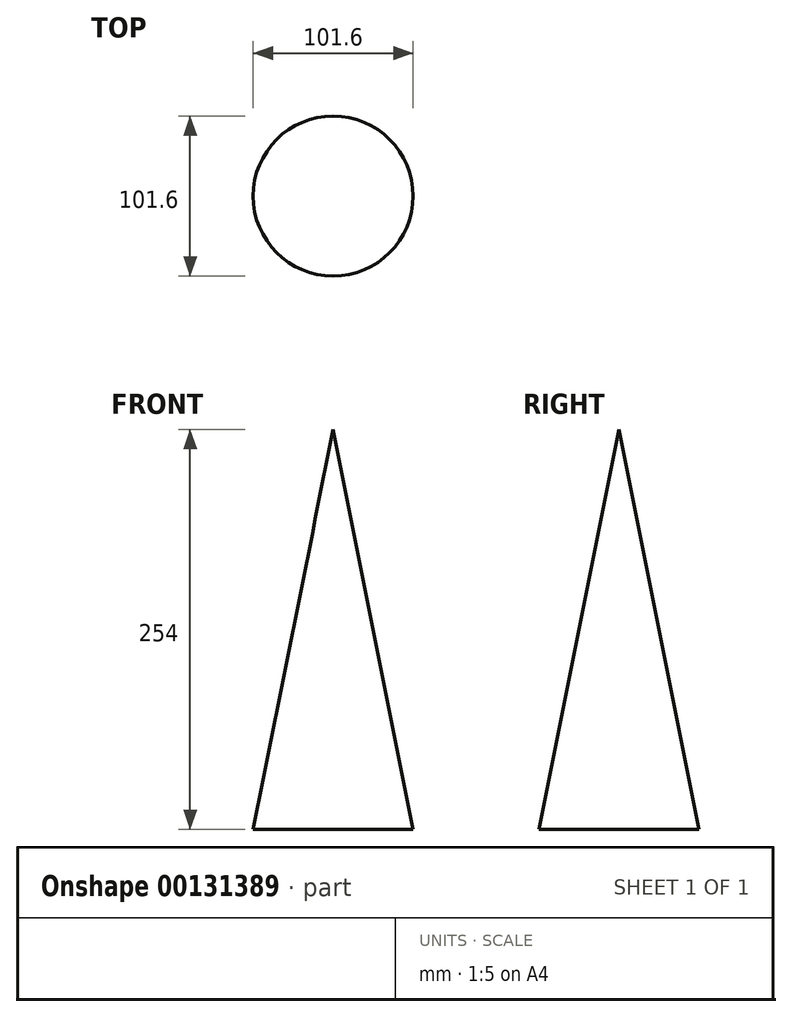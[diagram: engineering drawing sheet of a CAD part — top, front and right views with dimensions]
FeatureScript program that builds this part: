
annotation { "Feature Type Name" : "Feature", "Feature Type Description" : "" }
export const myFeature = defineFeature(function(context is Context, id is Id, definition is map)
    precondition{}
    {
        {
            var Q0;
            Q0=qCreatedBy(makeId("Front.planeOp"),FACE);
            var sketch = newSketch(context, id + "F0", { "sketchPlane" : qUnion([Q0])});
            skLineSegment(sketch, "E0", {"start": v(0, 132.51) * mm, "end": v(0, -121.49) * mm});
            skLineSegment(sketch, "E1", {"start": v(0, -121.49) * mm, "end": v(-50.8, -121.49) * mm});
            skLineSegment(sketch, "E2", {"start": v(0, 132.51) * mm, "end": v(-50.8, -121.49) * mm});
            skSolve(sketch);
        }
        {
            var Q0;
            Q0=makeQuery(id+"F0.imprint","IMPRINT",FACE,{"disambiguationData":[TD([[makeQuery(id+"F0.imprint","IMPRINT",EDGE,{"derivedFrom":sQuery(id+"F0.wireOp",EDGE,"E0")}),-1.0]])]});
            var Q1;
            Q1=sQuery(id+"F0.wireOp",EDGE,"E0");
            revolve(context, id + "F1", {"entities" : qUnion([Q0]), "axis" : qUnion([Q1]), "revolveType" : RevolveType.FULL});
        }
    });
